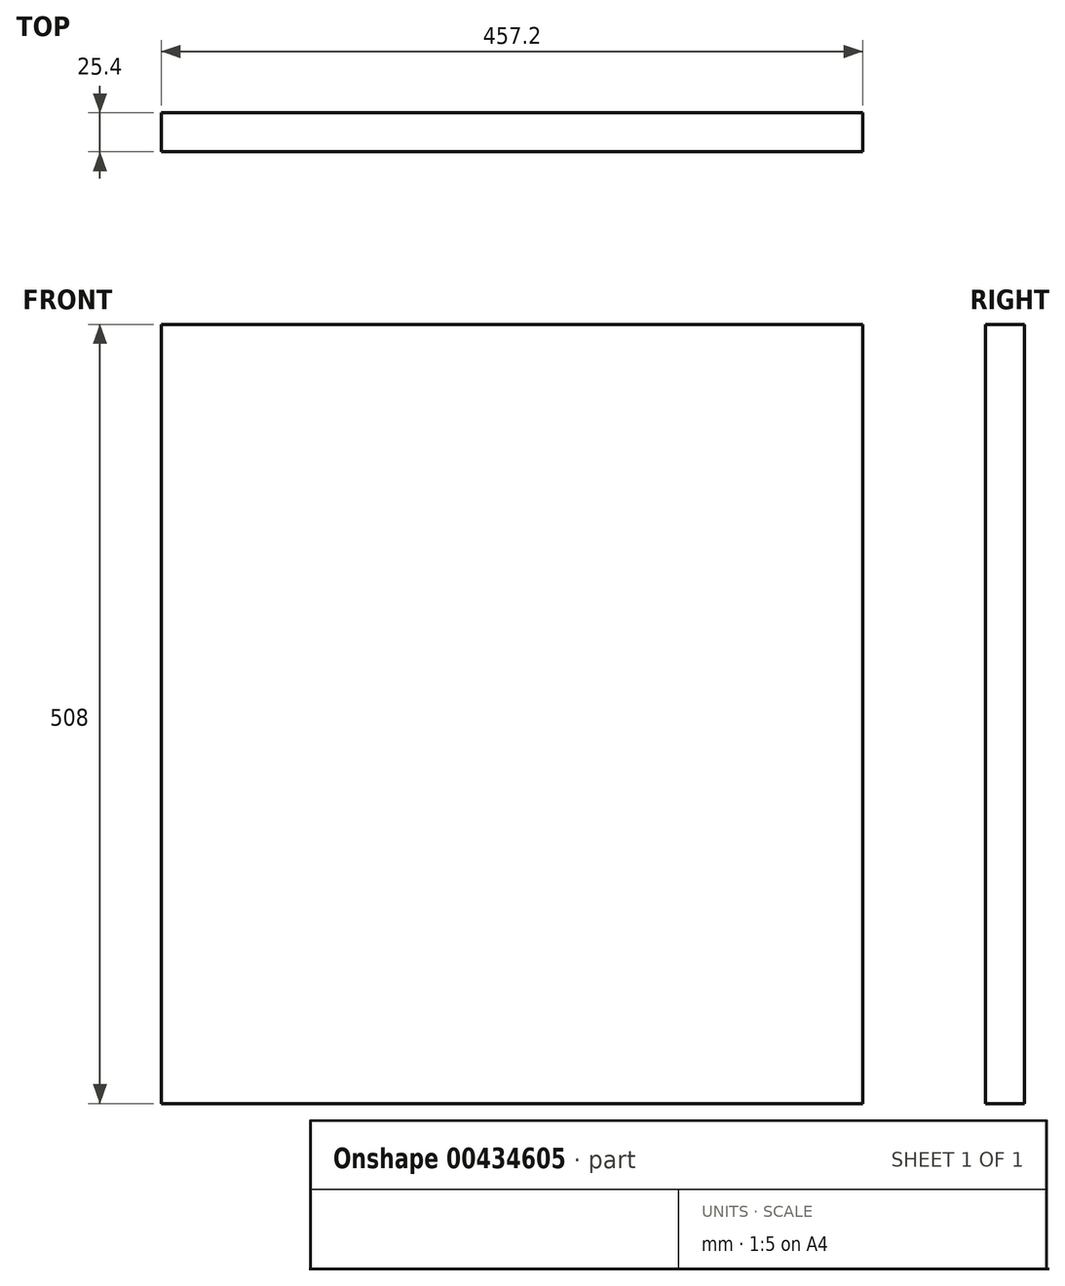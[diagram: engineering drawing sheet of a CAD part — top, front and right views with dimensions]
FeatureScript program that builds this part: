
annotation { "Feature Type Name" : "Feature", "Feature Type Description" : "" }
export const myFeature = defineFeature(function(context is Context, id is Id, definition is map)
    precondition{}
    {
        {
            var Q0;
            Q0=qCreatedBy(makeId("Front.planeOp"),FACE);
            var sketch = newSketch(context, id + "F0", { "sketchPlane" : qUnion([Q0])});
            skLineSegment(sketch, "E0.bottom", {"start": v(-218.35, 254) * mm, "end": v(238.85, 254) * mm});
            skLineSegment(sketch, "E0.top", {"start": v(-218.35, -254) * mm, "end": v(238.85, -254) * mm});
            skLineSegment(sketch, "E0.left", {"start": v(-218.35, 254) * mm, "end": v(-218.35, -254) * mm});
            skLineSegment(sketch, "E0.right", {"start": v(238.85, 254) * mm, "end": v(238.85, -254) * mm});
            skPoint(sketch, "E0.middle", {"position": v(10.25, 0) * mm});
            skSolve(sketch);
        }
        {
            var Q0;
            Q0=makeQuery(id+"F0.imprint","IMPRINT",FACE,{"disambiguationData":[TD([[makeQuery(id+"F0.imprint","IMPRINT",EDGE,{"derivedFrom":sQuery(id+"F0.wireOp",EDGE,"E0.bottom")}),-1.0]])]});
            extrude(context, id + "F1", {"entities" : qUnion([Q0]), "depth" : 25.4 * mm});
        }
    });
